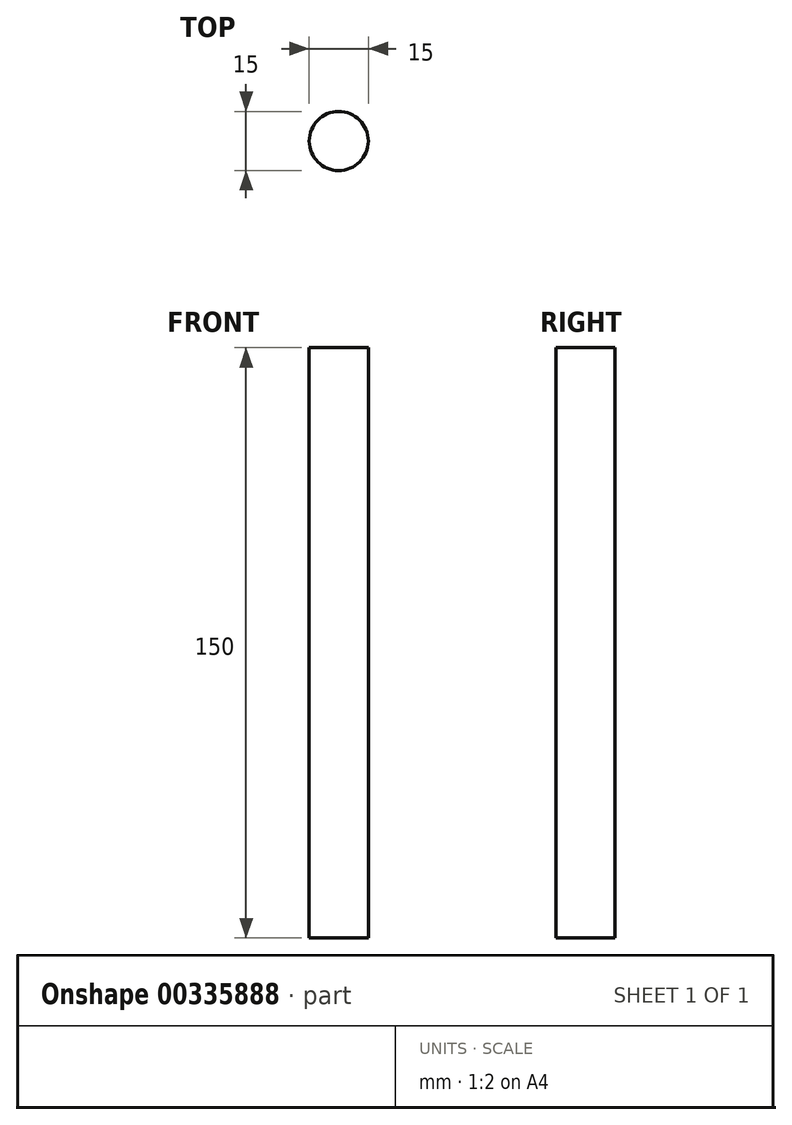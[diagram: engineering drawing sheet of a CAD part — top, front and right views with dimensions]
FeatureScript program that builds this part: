
annotation { "Feature Type Name" : "Feature", "Feature Type Description" : "" }
export const myFeature = defineFeature(function(context is Context, id is Id, definition is map)
    precondition{}
    {
        {
            assignVariable(context, id + "F0", {"name" : "lunghezza", "anyValue" : 150});
        }
        {
            var Q0;
            Q0=qCreatedBy(makeId("Top.planeOp"),FACE);
            var sketch = newSketch(context, id + "F1", { "sketchPlane" : qUnion([Q0])});
            skCircle(sketch, "E0", {"center": v(0, 0) * mm, "radius": 7.5 * mm});
            skSolve(sketch);
        }
        {
            var Q0;
            Q0 = qSketchRegion(id + "F1", true);
            extrude(context, id + "F2", {"entities" : qUnion([Q0]), "depth" : (getVariable(context, 'lunghezza')) * mm});
        }
    });
